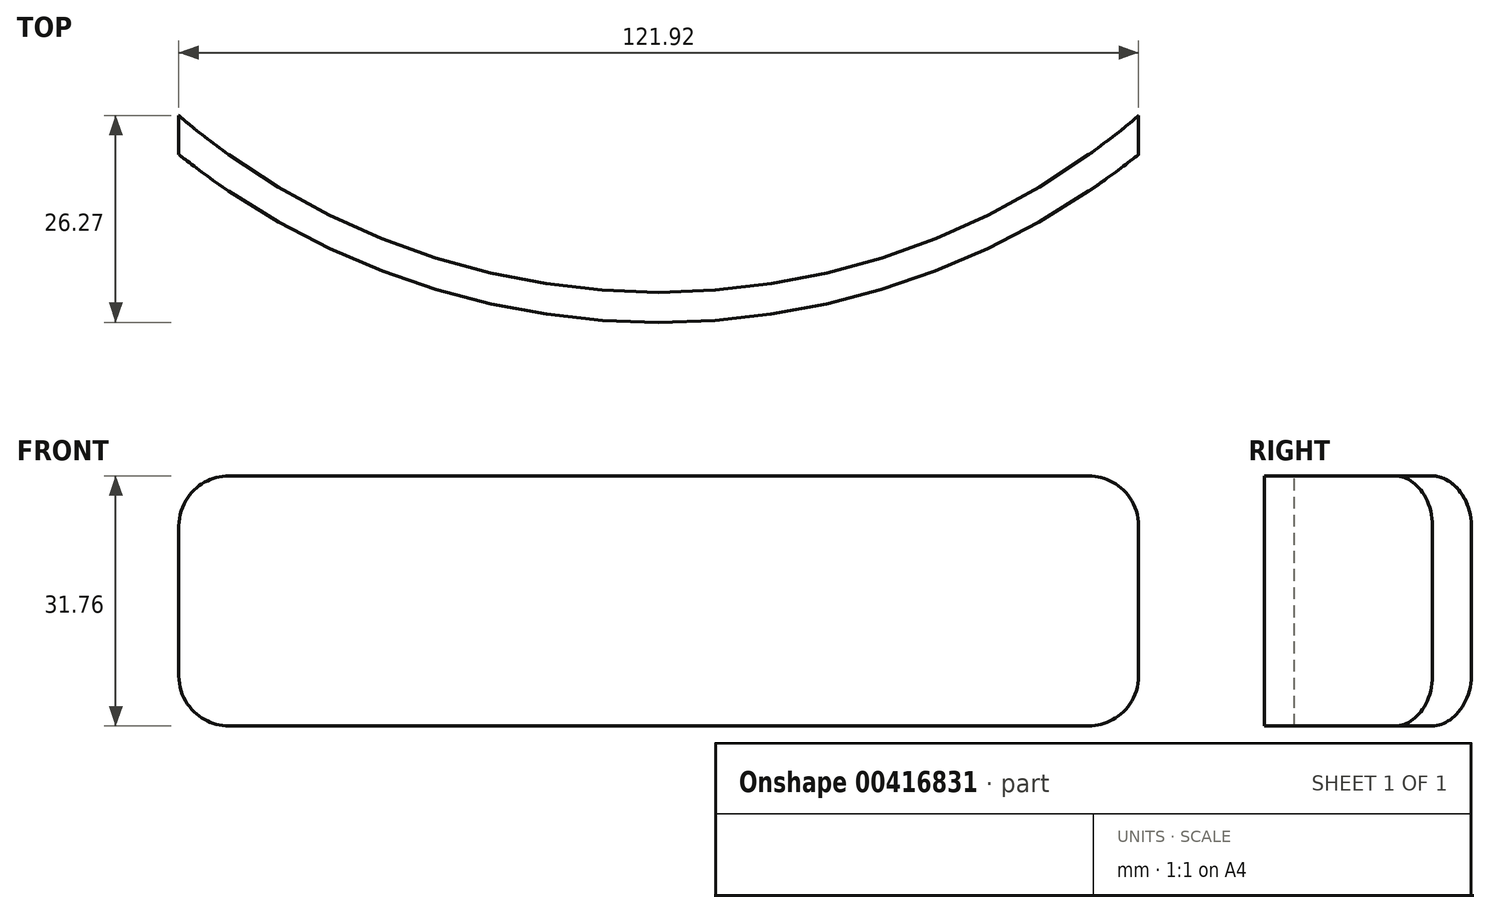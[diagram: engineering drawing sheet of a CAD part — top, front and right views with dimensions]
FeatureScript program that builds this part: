
annotation { "Feature Type Name" : "Feature", "Feature Type Description" : "" }
export const myFeature = defineFeature(function(context is Context, id is Id, definition is map)
    precondition{}
    {
        {
            var Q0;
            Q0=qCreatedBy(makeId("Front.planeOp"),FACE);
            var sketch = newSketch(context, id + "F0", { "sketchPlane" : qUnion([Q0])});
            skLineSegment(sketch, "E0.bottom", {"start": v(-54.6, 15.88) * mm, "end": v(54.6, 15.88) * mm});
            skLineSegment(sketch, "E0.top", {"start": v(-54.6, -15.87) * mm, "end": v(54.6, -15.87) * mm});
            skLineSegment(sketch, "E0.left", {"start": v(-60.96, 9.53) * mm, "end": v(-60.96, -9.52) * mm});
            skLineSegment(sketch, "E0.right", {"start": v(60.96, 9.52) * mm, "end": v(60.96, -9.52) * mm});
            skPoint(sketch, "E1.visualSharp", {"position": v(-60.96, 15.88) * mm});
            skArc(sketch, "E1.filletArc", {"start": v(-54.6, 15.88) * mm, "mid": v(-59.1, 14.02) * mm, "end": v(-60.96, 9.53) * mm});
            skPoint(sketch, "E2.visualSharp", {"position": v(-60.96, -15.87) * mm});
            skArc(sketch, "E2.filletArc", {"start": v(-60.96, -9.52) * mm, "mid": v(-59.1, -14.02) * mm, "end": v(-54.6, -15.88) * mm});
            skPoint(sketch, "E3.visualSharp", {"position": v(60.96, -15.87) * mm});
            skArc(sketch, "E3.filletArc", {"start": v(54.6, -15.87) * mm, "mid": v(59.1, -14.02) * mm, "end": v(60.96, -9.52) * mm});
            skPoint(sketch, "E4.visualSharp", {"position": v(60.96, 15.88) * mm});
            skArc(sketch, "E4.filletArc", {"start": v(60.96, 9.52) * mm, "mid": v(59.1, 14.02) * mm, "end": v(54.6, 15.88) * mm});
            skSolve(sketch);
        }
        {
            var Q0;
            Q0 = qSketchRegion(id + "F0", true);
            extrude(context, id + "F1", {"entities" : qUnion([Q0]), "depth" : 50.8 * mm, "offsetDistance" : 25.4 * mm});
        }
        {
            var Q0;
            Q0=makeQuery(id+"F1.opExtrude","SWEPT_FACE",FACE,{"disambiguationData":[OSD([sQuery(id+"F0.wireOp",EDGE,"E0.bottom")])]});
            var sketch = newSketch(context, id + "F2", { "sketchPlane" : qUnion([Q0])});
            skArc(sketch, "E5", {"start": v(-60.96, -7.93) * mm, "mid": v(0, -29.26) * mm, "end": v(60.96, -7.93) * mm});
            skArc(sketch, "E6", {"start": v(-60.96, -3) * mm, "mid": v(0, -25.45) * mm, "end": v(60.96, -3) * mm});
            skLineSegment(sketch, "E7", {"start": v(-60.96, -3) * mm, "end": v(-60.96, -7.93) * mm});
            skLineSegment(sketch, "E8", {"start": v(60.96, -7.93) * mm, "end": v(60.96, -3) * mm});
            skLineSegment(sketch, "E9", {"start": v(-60.96, -3) * mm, "end": v(-60.96, 0) * mm});
            skLineSegment(sketch, "E10", {"start": v(-60.96, 0) * mm, "end": v(60.96, 0) * mm});
            skLineSegment(sketch, "E11", {"start": v(60.96, 0) * mm, "end": v(60.96, -3) * mm});
            skLineSegment(sketch, "E12", {"start": v(60.96, -7.93) * mm, "end": v(60.96, -50.8) * mm});
            skLineSegment(sketch, "E13", {"start": v(60.96, -50.8) * mm, "end": v(-60.96, -50.8) * mm});
            skLineSegment(sketch, "E14", {"start": v(-60.96, -50.8) * mm, "end": v(-60.96, -7.93) * mm});
            skSolve(sketch);
        }
        {
            var Q0;
            {var subQ0=sQuery(id+"F2.wireOp",EDGE,"E14");Q0=makeQuery(id+"F2.imprint","IMPRINT",FACE,{"disambiguationData":[TD([[makeQuery(id+"F2.imprint","IMPRINT",EDGE,{"derivedFrom":subQ0}),-1.0]])]});}
            var Q1;
            {var subQ0=sQuery(id+"F2.wireOp",EDGE,"E12");Q1=makeQuery(id+"F2.imprint","IMPRINT",FACE,{"disambiguationData":[TD([[makeQuery(id+"F2.imprint","IMPRINT",EDGE,{"derivedFrom":subQ0}),-1.0]])]});}
            var Q2;
            {var subQ0=sQuery(id+"F2.wireOp",EDGE,"E9");Q2=makeQuery(id+"F2.imprint","IMPRINT",FACE,{"disambiguationData":[TD([[makeQuery(id+"F2.imprint","IMPRINT",EDGE,{"derivedFrom":subQ0}),-1.0]])]});}
            var Q3;
            {var subQ0=sQuery(id+"F2.wireOp",EDGE,"E11");Q3=makeQuery(id+"F2.imprint","IMPRINT",FACE,{"disambiguationData":[TD([[makeQuery(id+"F2.imprint","IMPRINT",EDGE,{"derivedFrom":subQ0}),-1.0]])]});}
            var Q4;
            {var subQ0=sQuery(id+"F2.wireOp",EDGE,"E5");var subQ1=sQuery(id+"F0.wireOp",EDGE,"E0.bottom");var subQ2=makeQuery(id+"F1.opExtrude","SWEPT_EDGE",EDGE,{"disambiguationData":[OSD([subQ1,sQuery(id+"F0.wireOp",EDGE,"E1.filletArc")])]});var subQ3=makeQuery(id+"F2.imprint","INTERSECT",VERTEX,{"derivedFrom":[subQ2,subQ0]});Q4=makeQuery(id+"F2.imprint","IMPRINT",FACE,{"disambiguationData":[TD([[makeQuery(id+"F2.imprint","IMPRINT",EDGE,{"disambiguationData":[TD([[subQ3,-1.0]])],"derivedFrom":subQ0}),-1.0]])]});}
            var Q5;
            {var subQ0=sQuery(id+"F2.wireOp",EDGE,"E6");var subQ1=sQuery(id+"F0.wireOp",EDGE,"E0.bottom");var subQ2=makeQuery(id+"F1.opExtrude","SWEPT_EDGE",EDGE,{"disambiguationData":[OSD([subQ1,sQuery(id+"F0.wireOp",EDGE,"E1.filletArc")])]});var subQ3=makeQuery(id+"F2.imprint","INTERSECT",VERTEX,{"derivedFrom":[subQ2,subQ0]});Q5=makeQuery(id+"F2.imprint","IMPRINT",FACE,{"disambiguationData":[TD([[makeQuery(id+"F2.imprint","IMPRINT",EDGE,{"disambiguationData":[TD([[subQ3,-1.0]])],"derivedFrom":subQ0}),1.0]])]});}
            extrude(context, id + "F3", {"entities" : qUnion([Q0, Q1, Q2, Q3, Q4, Q5]), "operationType" : NewBodyOperationType.REMOVE, "oppositeDirection" : true, "depth" : 50.8 * mm, "offsetDistance" : 25.4 * mm});
        }
    });
